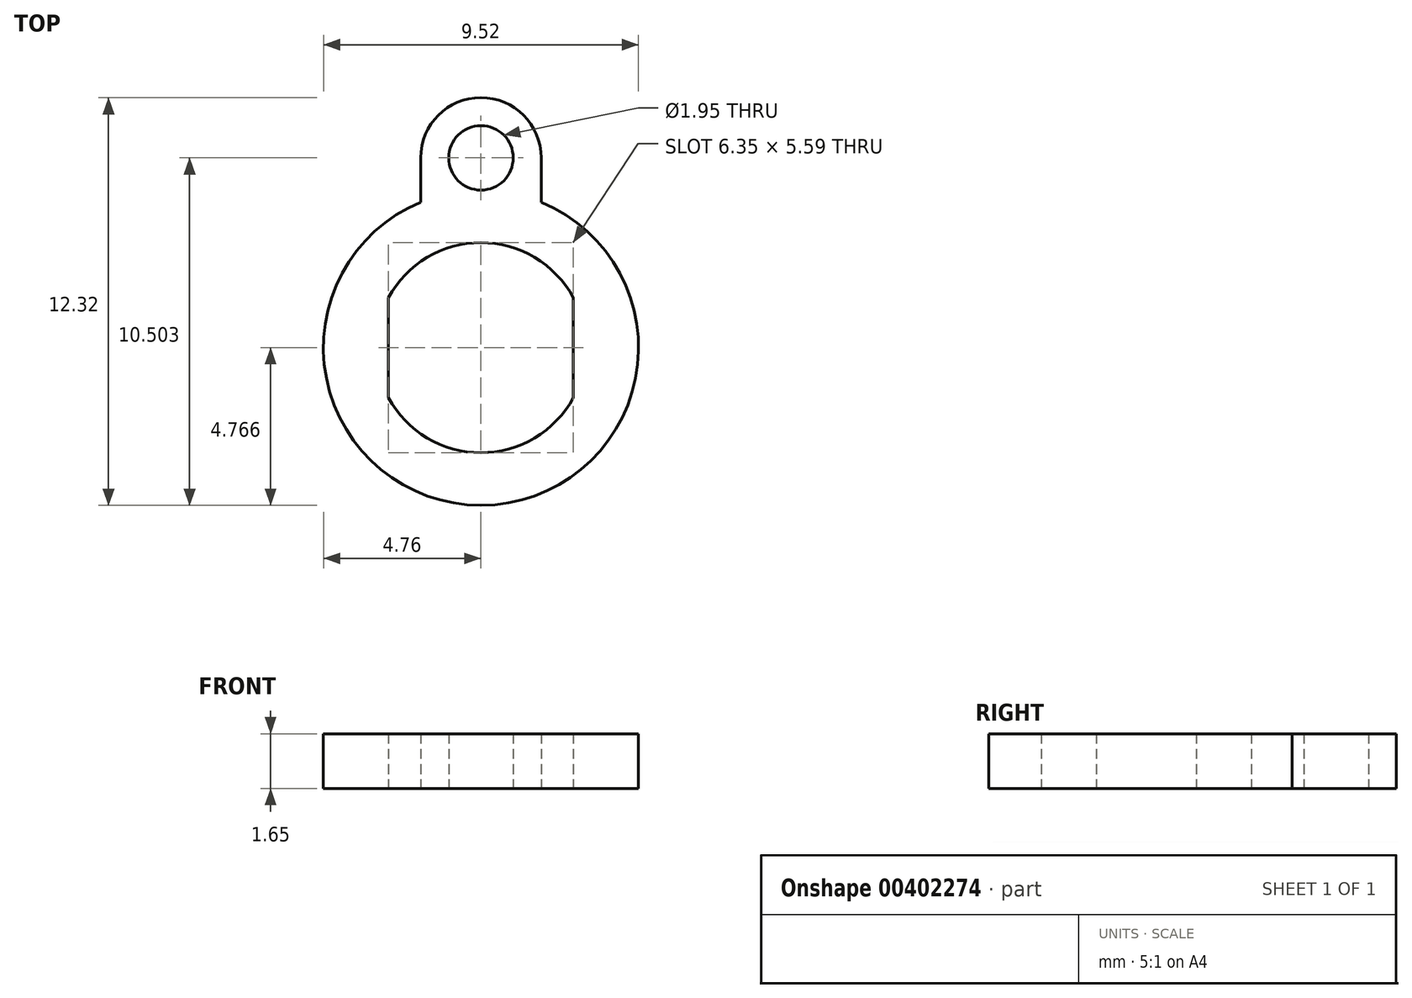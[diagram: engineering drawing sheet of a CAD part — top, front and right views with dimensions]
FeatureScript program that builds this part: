
annotation { "Feature Type Name" : "Feature", "Feature Type Description" : "" }
export const myFeature = defineFeature(function(context is Context, id is Id, definition is map)
    precondition{}
    {
        {
            var Q0;
            Q0=qCreatedBy(makeId("Top.planeOp"),FACE);
            var sketch = newSketch(context, id + "F0", { "sketchPlane" : qUnion([Q0])});
            skArc(sketch, "E0", {"start": v(2.8, 10.63) * mm, "mid": v(0, 12.3) * mm, "end": v(-2.8, 10.63) * mm});
            skCircle(sketch, "E1", {"center": v(0, 14.86) * mm, "radius": 0.97 * mm});
            skArc(sketch, "E2", {"start": v(1.82, 14.86) * mm, "mid": v(0, 16.68) * mm, "end": v(-1.82, 14.86) * mm});
            skLineSegment(sketch, "E3", {"start": v(-1.82, 14.86) * mm, "end": v(-1.82, 13.53) * mm});
            skLineSegment(sketch, "E4", {"start": v(1.82, 14.86) * mm, "end": v(1.82, 13.53) * mm});
            skLineSegment(sketch, "E5.0", {"start": v(2.8, 10.63) * mm, "end": v(2.8, 7.62) * mm});
            skLineSegment(sketch, "E6.trimOffspring", {"start": v(-2.8, 10.63) * mm, "end": v(-2.8, 7.62) * mm});
            skArc(sketch, "E7.trimOffspring", {"start": v(-2.8, 7.62) * mm, "mid": v(0, 5.95) * mm, "end": v(2.8, 7.62) * mm});
            skCircle(sketch, "E8.converted", {"center": v(0, 9.13) * mm, "radius": 4.76 * mm});
            skSolve(sketch);
        }
        {
            var Q0;
            Q0=makeQuery(id+"F0.imprint","IMPRINT",FACE,{"disambiguationData":[TD([[makeQuery(id+"F0.imprint","IMPRINT",EDGE,{"derivedFrom":sQuery(id+"F0.wireOp",EDGE,"E0")}),-1.0]])]});
            var Q1;
            {var subQ2=sQuery(id+"F0.wireOp",EDGE,"E1");Q1=makeQuery(id+"F0.imprint","IMPRINT",FACE,{"disambiguationData":[TD([[makeQuery(id+"F0.imprint","IMPRINT",EDGE,{"derivedFrom":subQ2}),-1.0]])]});}
            extrude(context, id + "F1", {"entities" : qUnion([Q0, Q1]), "depth" : 1.65 * mm});
        }
    });
